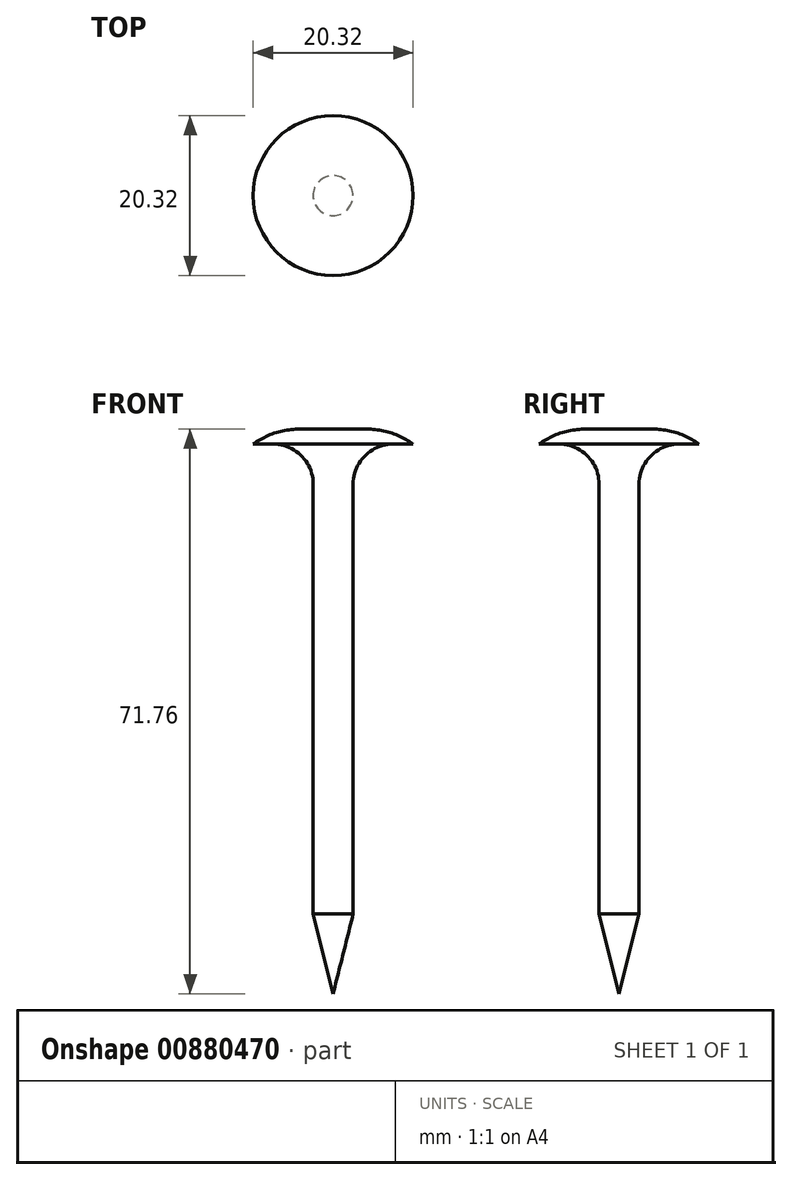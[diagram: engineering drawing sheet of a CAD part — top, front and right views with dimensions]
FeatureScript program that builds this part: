
annotation { "Feature Type Name" : "Feature", "Feature Type Description" : "" }
export const myFeature = defineFeature(function(context is Context, id is Id, definition is map)
    precondition{}
    {
        {
            var Q0;
            Q0=qCreatedBy(makeId("Front.planeOp"),FACE);
            var sketch = newSketch(context, id + "F0", { "sketchPlane" : qUnion([Q0])});
            skLineSegment(sketch, "E0.bottom", {"start": v(0, 12.7) * mm, "end": v(2.54, 12.7) * mm});
            skLineSegment(sketch, "E0.top", {"start": v(0, -57.15) * mm, "end": v(2.54, -57.15) * mm});
            skLineSegment(sketch, "E0.left", {"start": v(0, 12.7) * mm, "end": v(0, -57.15) * mm});
            skLineSegment(sketch, "E0.right", {"start": v(2.54, 12.7) * mm, "end": v(2.54, -57.15) * mm});
            skLineSegment(sketch, "E1.bottom", {"start": v(0, 14.6) * mm, "end": v(10.16, 14.6) * mm});
            skLineSegment(sketch, "E1.top", {"start": v(0, 12.7) * mm, "end": v(10.16, 12.7) * mm});
            skLineSegment(sketch, "E1.left", {"start": v(0, 14.6) * mm, "end": v(0, 12.7) * mm});
            skLineSegment(sketch, "E1.right", {"start": v(10.16, 14.6) * mm, "end": v(10.16, 12.7) * mm});
            skSolve(sketch);
        }
        {
            var Q0;
            Q0=qSketchRegion(id+"F0",true);
            var Q1;
            Q1=sQuery(id+"F0.wireOp",EDGE,"E0.left");
            revolve(context, id + "F1", {"entities" : qUnion([Q0]), "axis" : qUnion([Q1]), "revolveType" : RevolveType.FULL});
        }
        {
            var Q0;
            Q0=makeQuery(id+"F1.opRevolve","SWEPT_EDGE",EDGE,{"disambiguationData":[OSD([sQuery(id+"F0.wireOp",EDGE,"E0.top"),sQuery(id+"F0.wireOp",EDGE,"E0.right")])]});
            chamfer(context, id + "F2", {"entities" : qUnion([Q0]), "chamferType" : ChamferType.TWO_OFFSETS, "width1" : 10.16 * mm, "oppositeDirection" : false, "width2" : 2.54 * mm, "tangentPropagation" : true});
        }
        {
            var Q0;
            Q0=makeQuery(id+"F1.opRevolve","SWEPT_EDGE",EDGE,{"disambiguationData":[OSD([sQuery(id+"F0.wireOp",EDGE,"E0.right"),sQuery(id+"F0.wireOp",EDGE,"E1.top")])]});
            fillet(context, id + "F3", {"entities" : qUnion([Q0]), "radius" : 5.08 * mm, "tangentPropagation" : true, "allowEdgeOverflow" : false});
        }
        {
            var Q0;
            Q0=makeQuery(id+"F1.opRevolve","SWEPT_EDGE",EDGE,{"disambiguationData":[OSD([sQuery(id+"F0.wireOp",EDGE,"E1.bottom"),sQuery(id+"F0.wireOp",EDGE,"E1.right")])]});
            fillet(context, id + "F4", {"entities" : qUnion([Q0]), "radius" : 10.16 * mm, "tangentPropagation" : true, "allowEdgeOverflow" : false});
        }
    });
